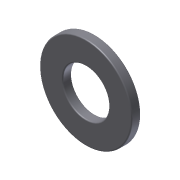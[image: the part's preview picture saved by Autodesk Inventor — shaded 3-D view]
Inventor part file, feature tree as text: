
AUTODESK INVENTOR PART (.ipt)
format: ipt  version: 2011 SP1 (Build 150282100, 282)  size: 108,032 bytes
history: native  units: in
note: dims shown in document units (in); Inventor stores cm internally (conversion verified against a paired STEP export)
features: extrude x1, fillet x1, sketch x1
ambient origin geometry x8: Origin, YZ Plane, XZ Plane, XY Plane, X Axis, Y Axis, Z Axis, Center Point
bodies: Solid1 (feature_tree)
feature tree (3):
  extrude  "Extrusion1"  Depth=0.812in
  fillet  "Fillet1"  Radius=0.08in
  sketch  "Sketch1"  dims[d0=0.406in d1=0.812in d2=0.08in d3=0.0in d4=0.01in]
